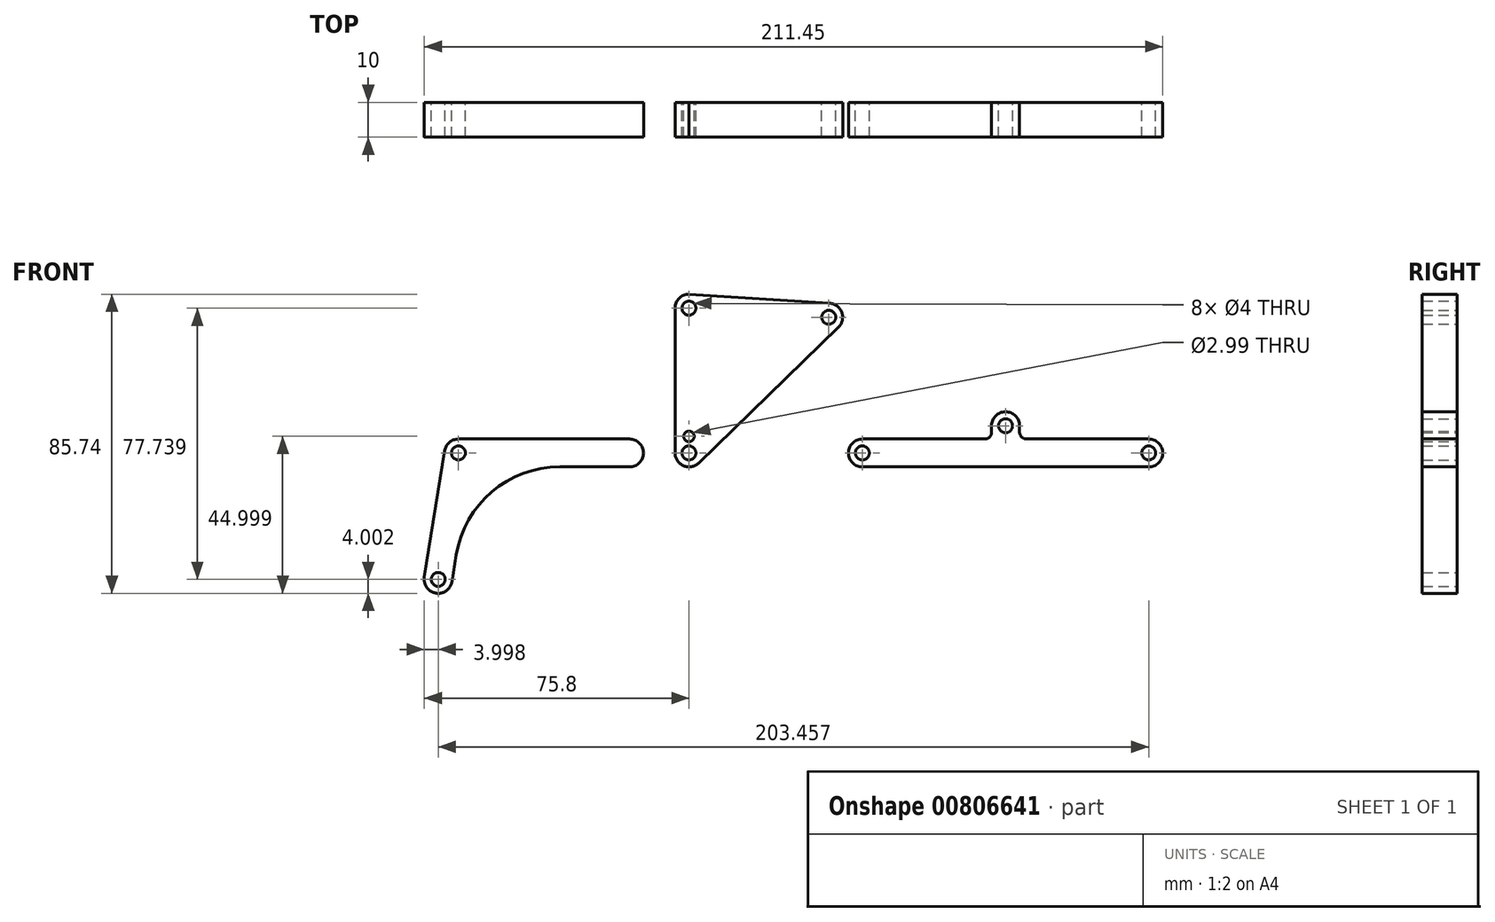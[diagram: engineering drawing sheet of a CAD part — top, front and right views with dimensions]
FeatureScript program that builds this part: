
annotation { "Feature Type Name" : "Feature", "Feature Type Description" : "" }
export const myFeature = defineFeature(function(context is Context, id is Id, definition is map)
    precondition{}
    {
        {
            var Q0;
            Q0=qCreatedBy(makeId("Front.planeOp"),FACE);
            var sketch = newSketch(context, id + "F0", { "sketchPlane" : qUnion([Q0])});
            skArc(sketch, "E0", {"start": v(0.52, 45.47) * mm, "mid": v(-2.64, 44.5) * mm, "end": v(-4, 41.5) * mm});
            skArc(sketch, "E1", {"start": v(-4, 0) * mm, "mid": v(-1.56, -3.68) * mm, "end": v(2.79, -2.87) * mm});
            skArc(sketch, "E2", {"start": v(42.8, 36.02) * mm, "mid": v(43.77, 40.28) * mm, "end": v(40.27, 42.88) * mm});
            skLineSegment(sketch, "E3", {"start": v(0, 45.5) * mm, "end": v(40.27, 42.88) * mm});
            skLineSegment(sketch, "E4", {"start": v(-4, 41.5) * mm, "end": v(-4, 0) * mm});
            skLineSegment(sketch, "E5", {"start": v(42.8, 36.02) * mm, "end": v(2.79, -2.87) * mm});
            skCircle(sketch, "E6", {"center": v(0, 41.5) * mm, "radius": 2 * mm});
            skCircle(sketch, "E7", {"center": v(0, 0) * mm, "radius": 2 * mm});
            skCircle(sketch, "E8", {"center": v(40.02, 38.9) * mm, "radius": 2 * mm});
            skCircle(sketch, "E9", {"center": v(0, 4.76) * mm, "radius": 1.5 * mm});
            skSolve(sketch);
        }
        {
            var Q0;
            Q0=makeQuery(id+"F0.imprint","IMPRINT",FACE,{"disambiguationData":[TD([[makeQuery(id+"F0.imprint","IMPRINT",EDGE,{"derivedFrom":sQuery(id+"F0.wireOp",EDGE,"E1")}),1.0]])]});
            extrude(context, id + "F1", {"entities" : qUnion([Q0]), "depth" : 10 * mm, "offsetDistance" : 25 * mm});
        }
        {
            var Q0;
            Q0=qCreatedBy(makeId("Front.planeOp"),FACE);
            var sketch = newSketch(context, id + "F2", { "sketchPlane" : qUnion([Q0])});
            skArc(sketch, "E10", {"start": v(-17, -4) * mm, "mid": v(-13, 0) * mm, "end": v(-17, 4) * mm});
            skArc(sketch, "E11", {"start": v(-75.75, -35.6) * mm, "mid": v(-72.43, -40.19) * mm, "end": v(-67.85, -36.87) * mm});
            skLineSegment(sketch, "E12", {"start": v(-75.75, -35.6) * mm, "end": v(-69.95, 0.63) * mm});
            skLineSegment(sketch, "E13", {"start": v(-66, 4) * mm, "end": v(-17, 4) * mm});
            skLineSegment(sketch, "E14", {"start": v(-67.85, -36.87) * mm, "end": v(-66.63, -29.26) * mm});
            skLineSegment(sketch, "E15", {"start": v(-17, -4) * mm, "end": v(-37.01, -4) * mm});
            skPoint(sketch, "E16.visualSharp", {"position": v(-62.59, -4) * mm});
            skArc(sketch, "E16.filletArc", {"start": v(-37.01, -4) * mm, "mid": v(-56.47, -11.17) * mm, "end": v(-66.63, -29.26) * mm});
            skCircle(sketch, "E17", {"center": v(-66, 0) * mm, "radius": 2 * mm});
            skCircle(sketch, "E18", {"center": v(-71.8, -36.24) * mm, "radius": 2 * mm});
            skArc(sketch, "E19", {"start": v(-66, 4) * mm, "mid": v(-68.6, 3.04) * mm, "end": v(-69.95, 0.63) * mm});
            skPoint(sketch, "E20.orphan", {"position": v(-70.05, 0) * mm});
            skSolve(sketch);
        }
        {
            var Q0;
            Q0=qCreatedBy(makeId("Front.planeOp"),FACE);
            var sketch = newSketch(context, id + "F3", { "sketchPlane" : qUnion([Q0])});
            skArc(sketch, "E21", {"start": v(49.65, 4) * mm, "mid": v(45.65, 0) * mm, "end": v(49.65, -4) * mm});
            skArc(sketch, "E22", {"start": v(94.65, 7.8) * mm, "mid": v(90.65, 11.8) * mm, "end": v(86.65, 7.8) * mm});
            skLineSegment(sketch, "E23", {"start": v(49.65, -4) * mm, "end": v(87.65, -4) * mm});
            skLineSegment(sketch, "E24", {"start": v(94.65, 7.8) * mm, "end": v(94.65, 6) * mm});
            skLineSegment(sketch, "E25", {"start": v(49.65, 4) * mm, "end": v(84.65, 4) * mm});
            skLineSegment(sketch, "E26", {"start": v(86.65, 7.8) * mm, "end": v(86.65, 6) * mm});
            skPoint(sketch, "E27.visualSharp", {"position": v(94.65, -4) * mm});
            skPoint(sketch, "E28.visualSharp", {"position": v(86.65, 4) * mm});
            skArc(sketch, "E28.filletArc", {"start": v(84.65, 4) * mm, "mid": v(86.07, 4.59) * mm, "end": v(86.65, 6) * mm});
            skCircle(sketch, "E29", {"center": v(49.65, 0) * mm, "radius": 2 * mm});
            skCircle(sketch, "E30", {"center": v(90.65, 7.8) * mm, "radius": 2 * mm});
            skLineSegment(sketch, "E31", {"start": v(90.65, 18.97) * mm, "end": v(90.65, -13) * mm, "construction": true});
            skArc(sketch, "E32.MirrorCS", {"start": v(96.65, 4) * mm, "mid": v(95.24, 4.59) * mm, "end": v(94.65, 6) * mm});
            skArc(sketch, "E33.MirrorCS", {"start": v(86.65, 7.8) * mm, "mid": v(90.65, 11.8) * mm, "end": v(94.65, 7.8) * mm});
            skLineSegment(sketch, "E34.MirrorCS", {"start": v(131.65, -4) * mm, "end": v(93.65, -4) * mm});
            skLineSegment(sketch, "E35.MirrorCS", {"start": v(131.65, 4) * mm, "end": v(96.65, 4) * mm});
            skCircle(sketch, "E36.MirrorC", {"center": v(131.65, 0) * mm, "radius": 2 * mm});
            skPoint(sketch, "E37.MirrorP", {"position": v(94.65, 4) * mm});
            skArc(sketch, "E38.MirrorCS", {"start": v(131.65, 4) * mm, "mid": v(135.65, 0) * mm, "end": v(131.65, -4) * mm});
            skLineSegment(sketch, "E39", {"start": v(87.65, -4) * mm, "end": v(93.65, -4) * mm});
            skSolve(sketch);
        }
        {
            var Q0;
            Q0=makeQuery(id+"F2.imprint","IMPRINT",FACE,{"disambiguationData":[TD([[makeQuery(id+"F2.imprint","IMPRINT",EDGE,{"derivedFrom":sQuery(id+"F2.wireOp",EDGE,"E10")}),1.0]])]});
            extrude(context, id + "F4", {"entities" : qUnion([Q0]), "depth" : 10 * mm, "offsetDistance" : 25 * mm});
        }
        {
            var Q0;
            Q0=makeQuery(id+"F3.imprint","IMPRINT",FACE,{"disambiguationData":[TD([[makeQuery(id+"F3.imprint","IMPRINT",EDGE,{"derivedFrom":sQuery(id+"F3.wireOp",EDGE,"E21")}),1.0]])]});
            extrude(context, id + "F5", {"entities" : qUnion([Q0]), "depth" : 10 * mm, "offsetDistance" : 25 * mm});
        }
    });
